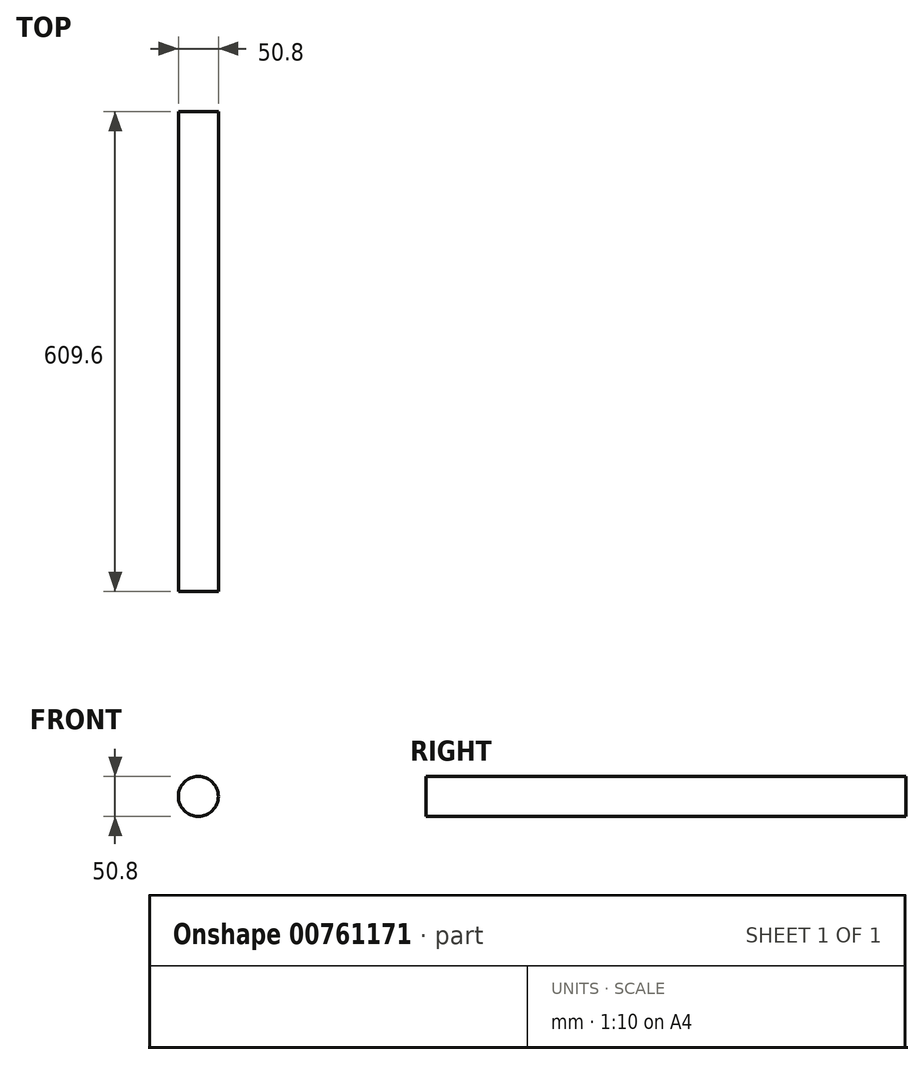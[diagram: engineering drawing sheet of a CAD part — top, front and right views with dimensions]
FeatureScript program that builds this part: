
annotation { "Feature Type Name" : "Feature", "Feature Type Description" : "" }
export const myFeature = defineFeature(function(context is Context, id is Id, definition is map)
    precondition{}
    {
        {
            var Q0;
            Q0=qCreatedBy(makeId("Front.planeOp"),FACE);
            var sketch = newSketch(context, id + "F0", { "sketchPlane" : qUnion([Q0])});
            skCircle(sketch, "E0", {"center": v(7.21, 32.21) * mm, "radius": 25.4 * mm});
            skSolve(sketch);
        }
        {
            var Q0;
            Q0=makeQuery(id+"F0.imprint","IMPRINT",FACE,{"disambiguationData":[TD([[makeQuery(id+"F0.imprint","IMPRINT",EDGE,{"derivedFrom":sQuery(id+"F0.wireOp",EDGE,"E0")}),1.0]])]});
            extrude(context, id + "F1", {"entities" : qUnion([Q0]), "depth" : 609.6 * mm, "offsetDistance" : 25.4 * mm});
        }
    });
